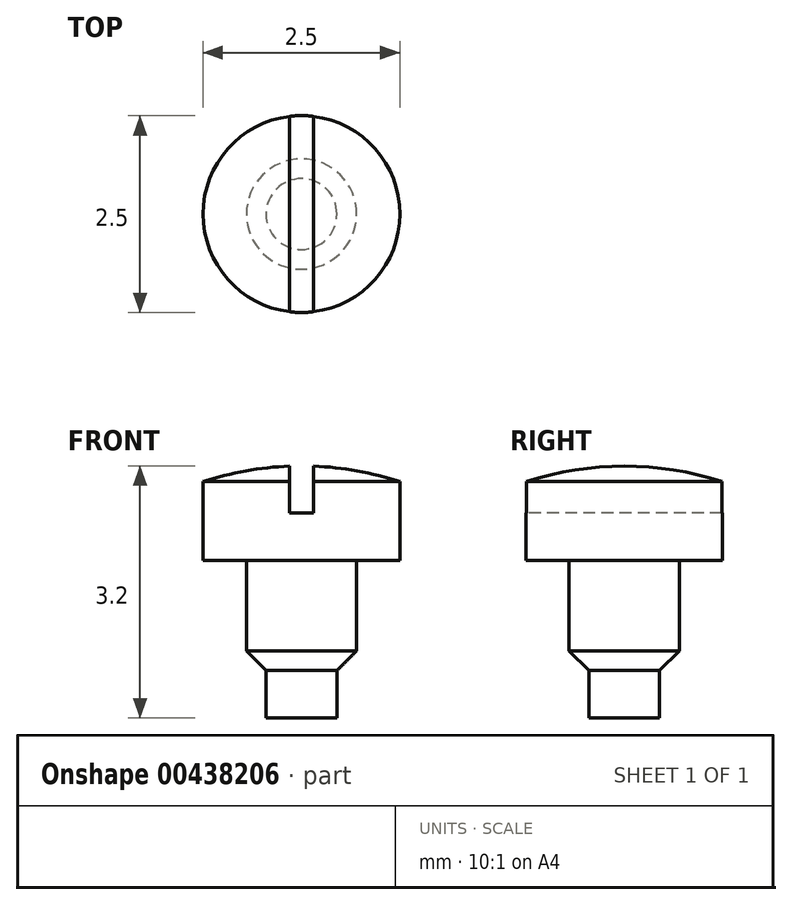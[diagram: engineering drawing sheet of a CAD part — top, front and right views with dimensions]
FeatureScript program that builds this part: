
annotation { "Feature Type Name" : "Feature", "Feature Type Description" : "" }
export const myFeature = defineFeature(function(context is Context, id is Id, definition is map)
    precondition{}
    {
        {
            var Q0;
            Q0=qCreatedBy(makeId("Front.planeOp"),FACE);
            var sketch = newSketch(context, id + "F0", { "sketchPlane" : qUnion([Q0])});
            skLineSegment(sketch, "E0", {"start": v(0, 0) * mm, "end": v(0.45, 0) * mm});
            skLineSegment(sketch, "E1", {"start": v(0.45, 0) * mm, "end": v(0.45, 0.6) * mm});
            skLineSegment(sketch, "E2", {"start": v(0.45, 0.6) * mm, "end": v(0.7, 0.85) * mm});
            skLineSegment(sketch, "E3", {"start": v(0.7, 0.85) * mm, "end": v(0.7, 2) * mm});
            skLineSegment(sketch, "E4", {"start": v(0.7, 2) * mm, "end": v(1.25, 2) * mm});
            skLineSegment(sketch, "E5", {"start": v(1.25, 2) * mm, "end": v(1.25, 3) * mm});
            skLineSegment(sketch, "E6", {"start": v(1.25, 3) * mm, "end": v(0, 3) * mm});
            skLineSegment(sketch, "E7", {"start": v(0, 3) * mm, "end": v(0, 0) * mm});
            skArc(sketch, "E8", {"start": v(1.25, 3) * mm, "mid": v(0.63, 3.15) * mm, "end": v(0, 3.2) * mm});
            skLineSegment(sketch, "E9", {"start": v(0, 3.2) * mm, "end": v(0, 3) * mm});
            skSolve(sketch);
        }
        {
            var Q0;
            {var subQ0=makeQuery(id+"F0.imprint","IMPRINT",EDGE,{"derivedFrom":sQuery(id+"F0.wireOp",EDGE,"E6")});Q0=qUnion([makeQuery(id+"F0.imprint","IMPRINT",FACE,{"disambiguationData":[TD([[makeQuery(id+"F0.imprint","IMPRINT",EDGE,{"derivedFrom":sQuery(id+"F0.wireOp",EDGE,"E0")}),1.0]])]}),makeQuery(id+"F0.imprint","IMPRINT",FACE,{"disambiguationData":[TD([[subQ0,-1.0]])]})]);}
            var Q1;
            Q1=sQuery(id+"F0.wireOp",EDGE,"E7");
            revolve(context, id + "F1", {"entities" : qUnion([Q0]), "axis" : qUnion([Q1]), "revolveType" : RevolveType.FULL});
        }
        {
            var Q0;
            Q0=qCreatedBy(makeId("Front.planeOp"),FACE);
            var sketch = newSketch(context, id + "F2", { "sketchPlane" : qUnion([Q0])});
            skLineSegment(sketch, "E10", {"start": v(-0.15, 2.6) * mm, "end": v(0.15, 2.6) * mm});
            skPoint(sketch, "E11", {"position": v(0, 2.6) * mm});
            skLineSegment(sketch, "E12", {"start": v(-0.15, 2.6) * mm, "end": v(-0.15, 3.25) * mm});
            skLineSegment(sketch, "E13", {"start": v(-0.15, 3.25) * mm, "end": v(0.15, 3.25) * mm});
            skLineSegment(sketch, "E14", {"start": v(0.15, 3.25) * mm, "end": v(0.15, 2.6) * mm});
            skSolve(sketch);
        }
        {
            var Q0;
            Q0=makeQuery(id+"F2.imprint","IMPRINT",FACE,{"disambiguationData":[TD([[makeQuery(id+"F2.imprint","IMPRINT",EDGE,{"derivedFrom":sQuery(id+"F2.wireOp",EDGE,"E10")}),1.0]])]});
            extrude(context, id + "F3", {"entities" : qUnion([Q0]), "operationType" : NewBodyOperationType.REMOVE, "endBound" : BoundingType.SYMMETRIC, "oppositeDirection" : true, "depth" : 25 * mm});
        }
    });
